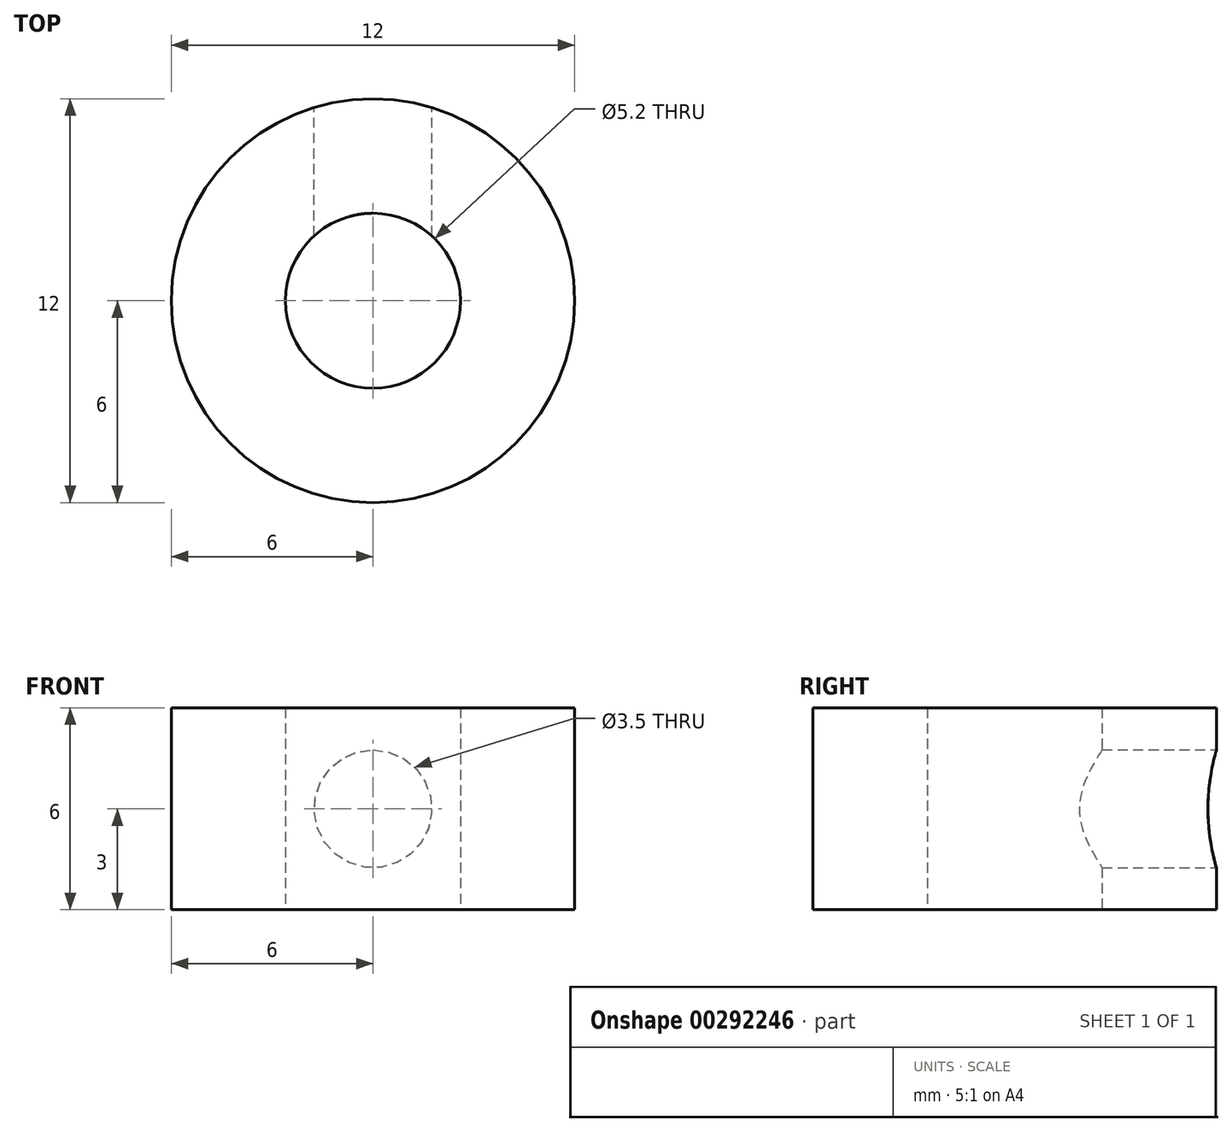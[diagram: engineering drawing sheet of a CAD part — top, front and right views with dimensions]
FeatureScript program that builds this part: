
annotation { "Feature Type Name" : "Feature", "Feature Type Description" : "" }
export const myFeature = defineFeature(function(context is Context, id is Id, definition is map)
    precondition{}
    {
        {
            var Q0;
            Q0=qCreatedBy(makeId("Top.planeOp"),FACE);
            var sketch = newSketch(context, id + "F0", { "sketchPlane" : qUnion([Q0])});
            skLineSegment(sketch, "E0", {"start": v(0, 0) * mm, "end": v(0, -12) * mm});
            skCircle(sketch, "E1", {"center": v(0, -6) * mm, "radius": 6 * mm});
            skCircle(sketch, "E2", {"center": v(0, -6) * mm, "radius": 2.6 * mm});
            skSolve(sketch);
        }
        {
            var Q0;
            Q0 = qSketchRegion(id + "F0", true);
            extrude(context, id + "F1", {"entities" : qUnion([Q0]), "depth" : 6 * mm});
        }
        {
            var Q0;
            Q0=qCreatedBy(makeId("Front.planeOp"),FACE);
            var sketch = newSketch(context, id + "F2", { "sketchPlane" : qUnion([Q0])});
            skLineSegment(sketch, "E3", {"start": v(0, 0) * mm, "end": v(0, 6) * mm});
            skCircle(sketch, "E4", {"center": v(0, 3) * mm, "radius": 1.75 * mm});
            skSolve(sketch);
        }
        {
            var Q0;
            Q0 = qSketchRegion(id + "F2", true);
            extrude(context, id + "F3", {"entities" : qUnion([Q0]), "operationType" : NewBodyOperationType.REMOVE, "depth" : 5.9 * mm});
        }
    });
